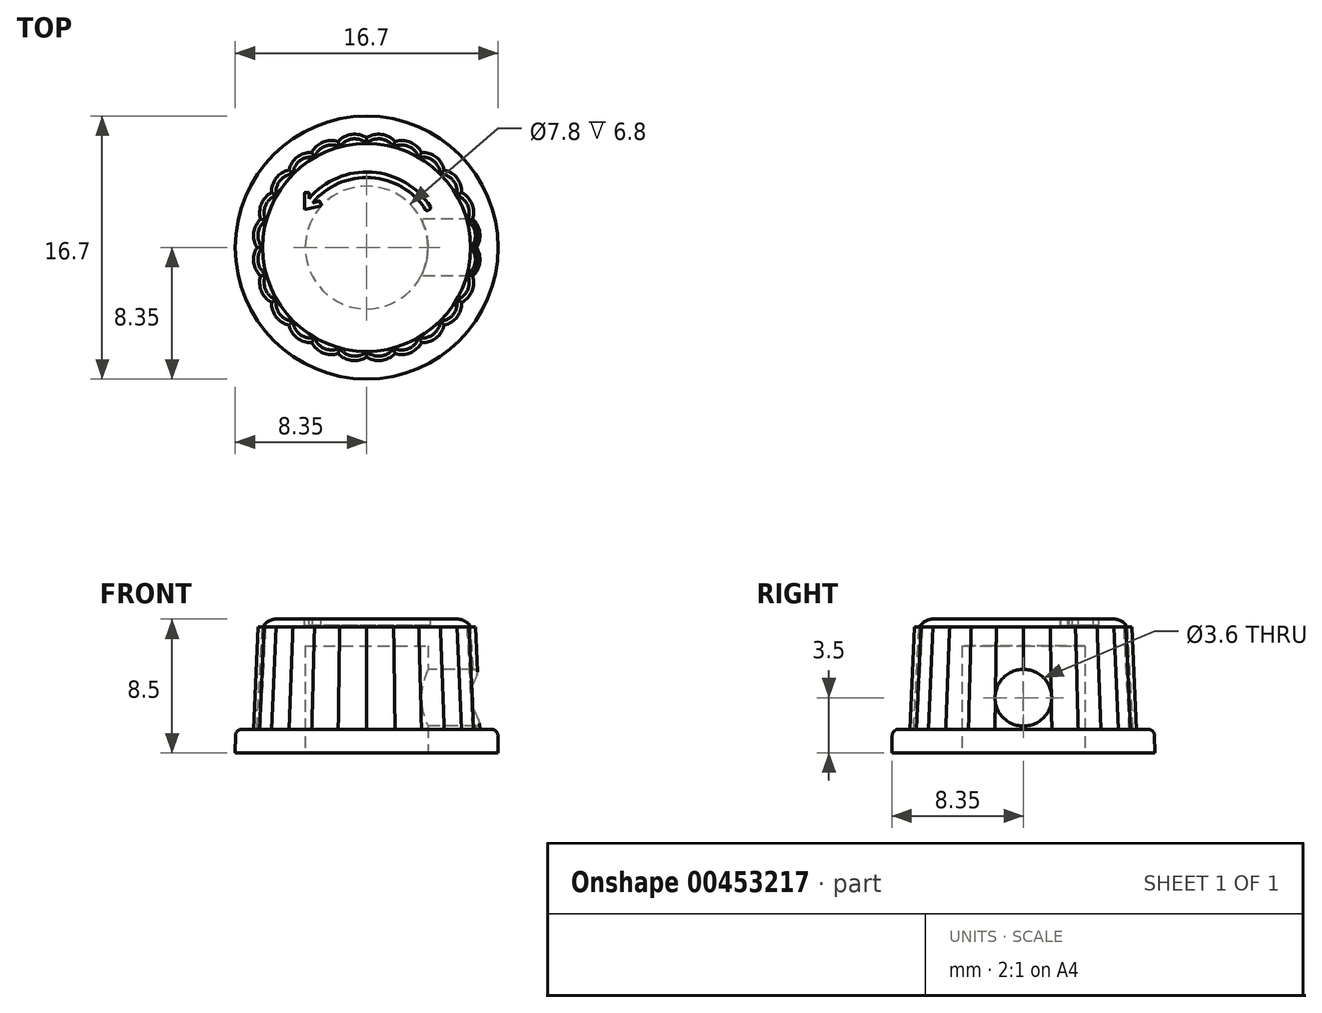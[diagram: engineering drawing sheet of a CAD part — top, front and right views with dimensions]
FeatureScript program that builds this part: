
annotation { "Feature Type Name" : "Feature", "Feature Type Description" : "" }
export const myFeature = defineFeature(function(context is Context, id is Id, definition is map)
    precondition{}
    {
        {
            var Q0;
            Q0=qCreatedBy(makeId("Top.planeOp"),FACE);
            var sketch = newSketch(context, id + "F0", { "sketchPlane" : qUnion([Q0])});
            skCircle(sketch, "E0", {"center": v(0, 0) * mm, "radius": 8.35 * mm});
            skSolve(sketch);
        }
        {
            var Q0;
            Q0=qSketchRegion(id+"F0",true);
            extrude(context, id + "F1", {"entities" : qUnion([Q0]), "depth" : 1.5 * mm, "hasDraft" : true, "draftAngle" : 1 * degree, "draftPullDirection" : true});
        }
        {
            var Q0;
            Q0=makeQuery(id+"F1.opExtrude","CAP_FACE",FACE,{"disambiguationData":[OSD([sQuery(id+"F0.wireOp",EDGE,"E0")])],"isStart":false});
            var sketch = newSketch(context, id + "F2", { "sketchPlane" : qUnion([Q0])});
            skCircle(sketch, "E1", {"center": v(0, 0) * mm, "radius": 6.9 * mm});
            skSolve(sketch);
        }
        {
            var Q0;
            Q0=qSketchRegion(id+"F2",true);
            extrude(context, id + "F3", {"entities" : qUnion([Q0]), "operationType" : NewBodyOperationType.ADD, "depth" : 6.5 * mm, "hasDraft" : true, "draftAngle" : 2.5 * degree, "draftPullDirection" : true});
        }
        {
            var Q0;
            Q0=makeQuery(id+"F3.opExtrude","CAP_FACE",FACE,{"disambiguationData":[OSD([sQuery(id+"F2.wireOp",EDGE,"E1")])],"isStart":false});
            var sketch = newSketch(context, id + "F4", { "sketchPlane" : qUnion([Q0])});
            skCircle(sketch, "E2", {"center": v(0, 0) * mm, "radius": 6.6 * mm});
            skSolve(sketch);
        }
        {
            var Q0;
            Q0=qSketchRegion(id+"F4",true);
            extrude(context, id + "F5", {"entities" : qUnion([Q0]), "operationType" : NewBodyOperationType.ADD, "depth" : .5 * mm});
        }
        {
            var Q0;
            Q0=makeQuery(id+"F3.opExtrude","CAP_FACE",FACE,{"disambiguationData":[OSD([sQuery(id+"F2.wireOp",EDGE,"E1")])],"isStart":false});
            var sketch = newSketch(context, id + "F6", { "sketchPlane" : qUnion([Q0])});
            skLineSegment(sketch, "E3", {"start": v(0, 0) * mm, "end": v(17.23, 0) * mm, "construction": true});
            skLineSegment(sketch, "E4", {"start": v(0, 0) * mm, "end": v(18.83, 5.05) * mm, "construction": true});
            skArc(sketch, "E5", {"start": v(6.62, 0) * mm, "mid": v(6.9, 0.9) * mm, "end": v(6.4, 1.71) * mm});
            skArc(sketch, "E6.1.0", {"start": v(6.4, -1.71) * mm, "mid": v(6.9, -0.9) * mm, "end": v(6.62, 0) * mm});
            skArc(sketch, "E6.2.0", {"start": v(5.73, -3.3) * mm, "mid": v(6.43, -2.66) * mm, "end": v(6.4, -1.71) * mm});
            skArc(sketch, "E6.3.0", {"start": v(4.68, -4.68) * mm, "mid": v(5.52, -4.23) * mm, "end": v(5.73, -3.3) * mm});
            skArc(sketch, "E6.4.0", {"start": v(3.3, -5.73) * mm, "mid": v(4.23, -5.52) * mm, "end": v(4.68, -4.68) * mm});
            skArc(sketch, "E6.5.0", {"start": v(1.71, -6.4) * mm, "mid": v(2.66, -6.43) * mm, "end": v(3.3, -5.73) * mm});
            skArc(sketch, "E6.6.0", {"start": v(0, -6.62) * mm, "mid": v(0.9, -6.9) * mm, "end": v(1.71, -6.4) * mm});
            skArc(sketch, "E6.7.0", {"start": v(-1.71, -6.4) * mm, "mid": v(-0.9, -6.9) * mm, "end": v(0, -6.62) * mm});
            skArc(sketch, "E6.8.0", {"start": v(-3.3, -5.73) * mm, "mid": v(-2.66, -6.43) * mm, "end": v(-1.71, -6.4) * mm});
            skArc(sketch, "E6.9.0", {"start": v(-4.68, -4.68) * mm, "mid": v(-4.23, -5.52) * mm, "end": v(-3.3, -5.73) * mm});
            skArc(sketch, "E6.10.0", {"start": v(-5.73, -3.3) * mm, "mid": v(-5.52, -4.23) * mm, "end": v(-4.68, -4.68) * mm});
            skArc(sketch, "E6.11.0", {"start": v(-6.4, -1.71) * mm, "mid": v(-6.43, -2.66) * mm, "end": v(-5.73, -3.3) * mm});
            skArc(sketch, "E6.12.0", {"start": v(-6.62, 0) * mm, "mid": v(-6.9, -0.9) * mm, "end": v(-6.4, -1.71) * mm});
            skArc(sketch, "E6.13.0", {"start": v(-6.4, 1.71) * mm, "mid": v(-6.9, 0.9) * mm, "end": v(-6.62, 0) * mm});
            skArc(sketch, "E6.14.0", {"start": v(-5.73, 3.3) * mm, "mid": v(-6.43, 2.66) * mm, "end": v(-6.4, 1.71) * mm});
            skArc(sketch, "E6.15.0", {"start": v(-4.68, 4.68) * mm, "mid": v(-5.52, 4.23) * mm, "end": v(-5.73, 3.3) * mm});
            skArc(sketch, "E6.16.0", {"start": v(-3.3, 5.73) * mm, "mid": v(-4.23, 5.52) * mm, "end": v(-4.68, 4.68) * mm});
            skArc(sketch, "E6.17.0", {"start": v(-1.71, 6.4) * mm, "mid": v(-2.66, 6.43) * mm, "end": v(-3.3, 5.73) * mm});
            skArc(sketch, "E6.18.0", {"start": v(0, 6.62) * mm, "mid": v(-0.9, 6.9) * mm, "end": v(-1.71, 6.4) * mm});
            skArc(sketch, "E6.19.0", {"start": v(1.71, 6.4) * mm, "mid": v(0.9, 6.9) * mm, "end": v(0, 6.62) * mm});
            skArc(sketch, "E6.20.0", {"start": v(3.3, 5.73) * mm, "mid": v(2.66, 6.43) * mm, "end": v(1.71, 6.4) * mm});
            skArc(sketch, "E6.21.0", {"start": v(4.68, 4.68) * mm, "mid": v(4.23, 5.52) * mm, "end": v(3.3, 5.73) * mm});
            skArc(sketch, "E6.22.0", {"start": v(5.73, 3.3) * mm, "mid": v(5.52, 4.23) * mm, "end": v(4.68, 4.68) * mm});
            skArc(sketch, "E6.23.0", {"start": v(6.4, 1.71) * mm, "mid": v(6.43, 2.66) * mm, "end": v(5.73, 3.3) * mm});
            skPoint(sketch, "E6.center", {"position": v(0, 0) * mm});
            skLineSegment(sketch, "E6.anchor1", {"start": v(0, 0) * mm, "end": v(6.62, 0) * mm, "construction": true});
            skLineSegment(sketch, "E6.anchor2", {"start": v(0, 0) * mm, "end": v(6.4, 1.71) * mm, "construction": true});
            skSolve(sketch);
        }
        {
            var Q0;
            Q0=qSketchRegion(id+"F6",true);
            var Q1;
            Q1=makeQuery(id+"F1.opExtrude","CAP_FACE",FACE,{"disambiguationData":[OSD([sQuery(id+"F0.wireOp",EDGE,"E0")])],"isStart":false});
            extrude(context, id + "F7", {"entities" : qUnion([Q0]), "operationType" : NewBodyOperationType.ADD, "endBound" : BoundingType.UP_TO_SURFACE, "oppositeDirection" : true, "endBoundEntityFace" : qUnion([Q1]), "depth" : 25 * mm, "hasDraft" : true, "draftAngle" : 2.5 * degree});
        }
        {
            var Q0;
            Q0=makeQuery(id+"F5.opExtrude","CAP_EDGE",EDGE,{"disambiguationData":[OSD([sQuery(id+"F4.wireOp",EDGE,"E2")])],"isStart":false});
            fillet(context, id + "F8", {"entities" : qUnion([Q0]), "radius" : 1 * mm, "tangentPropagation" : true, "allowEdgeOverflow" : false});
        }
        {
            var Q0;
            Q0=makeQuery(id+"F1.opExtrude","CAP_EDGE",EDGE,{"disambiguationData":[OSD([sQuery(id+"F0.wireOp",EDGE,"E0")])],"isStart":false});
            fillet(context, id + "F9", {"entities" : qUnion([Q0]), "radius" : .4 * mm, "tangentPropagation" : true, "allowEdgeOverflow" : false});
        }
        {
            var Q0;
            Q0=makeQuery(id+"F1.opExtrude","CAP_FACE",FACE,{"disambiguationData":[OSD([sQuery(id+"F0.wireOp",EDGE,"E0")])],"isStart":true});
            var sketch = newSketch(context, id + "F10", { "sketchPlane" : qUnion([Q0])});
            skCircle(sketch, "E7", {"center": v(0, 0) * mm, "radius": 3.9 * mm});
            skSolve(sketch);
        }
        {
            var Q0;
            Q0=qSketchRegion(id+"F10",true);
            extrude(context, id + "F11", {"entities" : qUnion([Q0]), "operationType" : NewBodyOperationType.REMOVE, "oppositeDirection" : true, "offsetDistance" : 25 * mm, "depth" : 6.8 * mm});
        }
        {
            var Q0;
            Q0=qCreatedBy(makeId("Right.planeOp"),FACE);
            var sketch = newSketch(context, id + "F12", { "sketchPlane" : qUnion([Q0])});
            skCircle(sketch, "E8", {"center": v(0, 3.5) * mm, "radius": 1.8 * mm});
            skSolve(sketch);
        }
        {
            var Q0;
            Q0=qSketchRegion(id+"F12",true);
            extrude(context, id + "F13", {"entities" : qUnion([Q0]), "operationType" : NewBodyOperationType.REMOVE, "depth" : 25 * mm});
        }
        {
            var Q0;
            Q0=makeQuery(id+"F5.opExtrude","CAP_FACE",FACE,{"disambiguationData":[OSD([sQuery(id+"F4.wireOp",EDGE,"E2")])],"isStart":false});
            var sketch = newSketch(context, id + "F14", { "sketchPlane" : qUnion([Q0])});
            skArc(sketch, "E9", {"start": v(4.05, 2.58) * mm, "mid": v(0.09, 4.8) * mm, "end": v(-3.96, 2.72) * mm});
            skArc(sketch, "E10", {"start": v(3.75, 2.39) * mm, "mid": v(0.04, 4.45) * mm, "end": v(-3.7, 2.46) * mm});
            skLineSegment(sketch, "E11", {"start": v(3.89, 2.36) * mm, "end": v(4.02, 2.44) * mm});
            skLineSegment(sketch, "E12.MirrorCS", {"start": v(-3.8, 2.3) * mm, "end": v(-4.1, 2.49) * mm, "construction": true});
            skPoint(sketch, "E13.orphan", {"position": v(-7.7, 4.66) * mm});
            skPoint(sketch, "E14.orphan", {"position": v(7.7, 4.66) * mm});
            skLineSegment(sketch, "E15", {"start": v(-3.96, 2.4) * mm, "end": v(-3.35, 3.17) * mm, "construction": true});
            skLineSegment(sketch, "E16", {"start": v(-3.96, 2.4) * mm, "end": v(-3.96, 3.44) * mm});
            skLineSegment(sketch, "E17.0", {"start": v(-3.66, 2.78) * mm, "end": v(-3.66, 3.44) * mm});
            skLineSegment(sketch, "E18", {"start": v(-3.9, 3.5) * mm, "end": v(-3.72, 3.5) * mm});
            skLineSegment(sketch, "E19.MirrorCS", {"start": v(-3.66, 2.78) * mm, "end": v(-3.02, 2.94) * mm});
            skLineSegment(sketch, "E20.MirrorCS", {"start": v(-2.89, 2.66) * mm, "end": v(-2.96, 2.95) * mm});
            skLineSegment(sketch, "E21.MirrorCS", {"start": v(-2.9, 2.72) * mm, "end": v(-2.94, 2.9) * mm});
            skLineSegment(sketch, "E22.MirrorCS", {"start": v(-3.96, 2.4) * mm, "end": v(-2.94, 2.64) * mm});
            skLineSegment(sketch, "E23.bottom", {"start": v(0.65, -0.5) * mm, "end": v(-0.65, -0.5) * mm});
            skLineSegment(sketch, "E23.top", {"start": v(-0.55, 2) * mm, "end": v(-0.65, 2) * mm});
            skLineSegment(sketch, "E23.left", {"start": v(0.75, -0.4) * mm, "end": v(0.75, -0.3) * mm});
            skLineSegment(sketch, "E23.right", {"start": v(-0.75, -0.4) * mm, "end": v(-0.75, 1.9) * mm});
            skPoint(sketch, "E23.middle", {"position": v(0, 0.75) * mm});
            skLineSegment(sketch, "E24", {"start": v(-0.45, 1.9) * mm, "end": v(-0.45, -0.15) * mm, "construction": true});
            skLineSegment(sketch, "E25", {"start": v(-0.4, -0.2) * mm, "end": v(0.65, -0.2) * mm});
            skPoint(sketch, "E26.orphan", {"position": v(0.75, 2) * mm});
            skPoint(sketch, "E27.visualSharp", {"position": v(-0.75, 2) * mm});
            skArc(sketch, "E27.filletArc", {"start": v(-0.65, 2) * mm, "mid": v(-0.72, 1.97) * mm, "end": v(-0.75, 1.9) * mm});
            skPoint(sketch, "E28.visualSharp", {"position": v(-0.45, 2) * mm});
            skArc(sketch, "E28.filletArc", {"start": v(-0.45, 1.9) * mm, "mid": v(-0.48, 1.97) * mm, "end": v(-0.55, 2) * mm});
            skPoint(sketch, "E29.visualSharp", {"position": v(0.75, -0.2) * mm});
            skArc(sketch, "E29.filletArc", {"start": v(0.75, -0.3) * mm, "mid": v(0.72, -0.23) * mm, "end": v(0.65, -0.2) * mm});
            skPoint(sketch, "E30.visualSharp", {"position": v(0.75, -0.5) * mm});
            skArc(sketch, "E30.filletArc", {"start": v(0.65, -0.5) * mm, "mid": v(0.72, -0.47) * mm, "end": v(0.75, -0.4) * mm});
            skPoint(sketch, "E31.visualSharp", {"position": v(-0.75, -0.5) * mm});
            skArc(sketch, "E31.filletArc", {"start": v(-0.75, -0.4) * mm, "mid": v(-0.72, -0.47) * mm, "end": v(-0.65, -0.5) * mm});
            skPoint(sketch, "E32.visualSharp", {"position": v(-0.45, -0.2) * mm});
            skArc(sketch, "E32.filletArc", {"start": v(-0.45, -0.15) * mm, "mid": v(-0.44, -0.19) * mm, "end": v(-0.4, -0.2) * mm});
            skPoint(sketch, "E33.visualSharp", {"position": v(3.8, 2.3) * mm});
            skArc(sketch, "E33.filletArc", {"start": v(3.75, 2.39) * mm, "mid": v(3.82, 2.35) * mm, "end": v(3.89, 2.36) * mm});
            skPoint(sketch, "E34.visualSharp", {"position": v(4.1, 2.49) * mm});
            skArc(sketch, "E34.filletArc", {"start": v(4.02, 2.44) * mm, "mid": v(4.06, 2.5) * mm, "end": v(4.05, 2.58) * mm});
            skPoint(sketch, "E35.visualSharp", {"position": v(-3.96, 3.5) * mm});
            skArc(sketch, "E35.filletArc", {"start": v(-3.9, 3.5) * mm, "mid": v(-3.94, 3.48) * mm, "end": v(-3.96, 3.44) * mm});
            skPoint(sketch, "E36.visualSharp", {"position": v(-3.66, 3.5) * mm});
            skArc(sketch, "E36.filletArc", {"start": v(-3.66, 3.44) * mm, "mid": v(-3.67, 3.48) * mm, "end": v(-3.72, 3.5) * mm});
            skPoint(sketch, "E37.visualSharp", {"position": v(-2.96, 2.95) * mm});
            skArc(sketch, "E37.filletArc", {"start": v(-2.94, 2.9) * mm, "mid": v(-2.97, 2.93) * mm, "end": v(-3.02, 2.94) * mm});
            skPoint(sketch, "E38.visualSharp", {"position": v(-2.89, 2.66) * mm});
            skArc(sketch, "E38.filletArc", {"start": v(-2.94, 2.64) * mm, "mid": v(-2.9, 2.67) * mm, "end": v(-2.9, 2.72) * mm});
            skSolve(sketch);
        }
        {
            var Q0;
            Q0=qSketchRegion(id+"F14",true);
            extrude(context, id + "F15", {"entities" : qUnion([Q0]), "operationType" : NewBodyOperationType.REMOVE, "oppositeDirection" : true, "offsetDistance" : 25 * mm, "depth" : .4 * mm});
        }
    });
